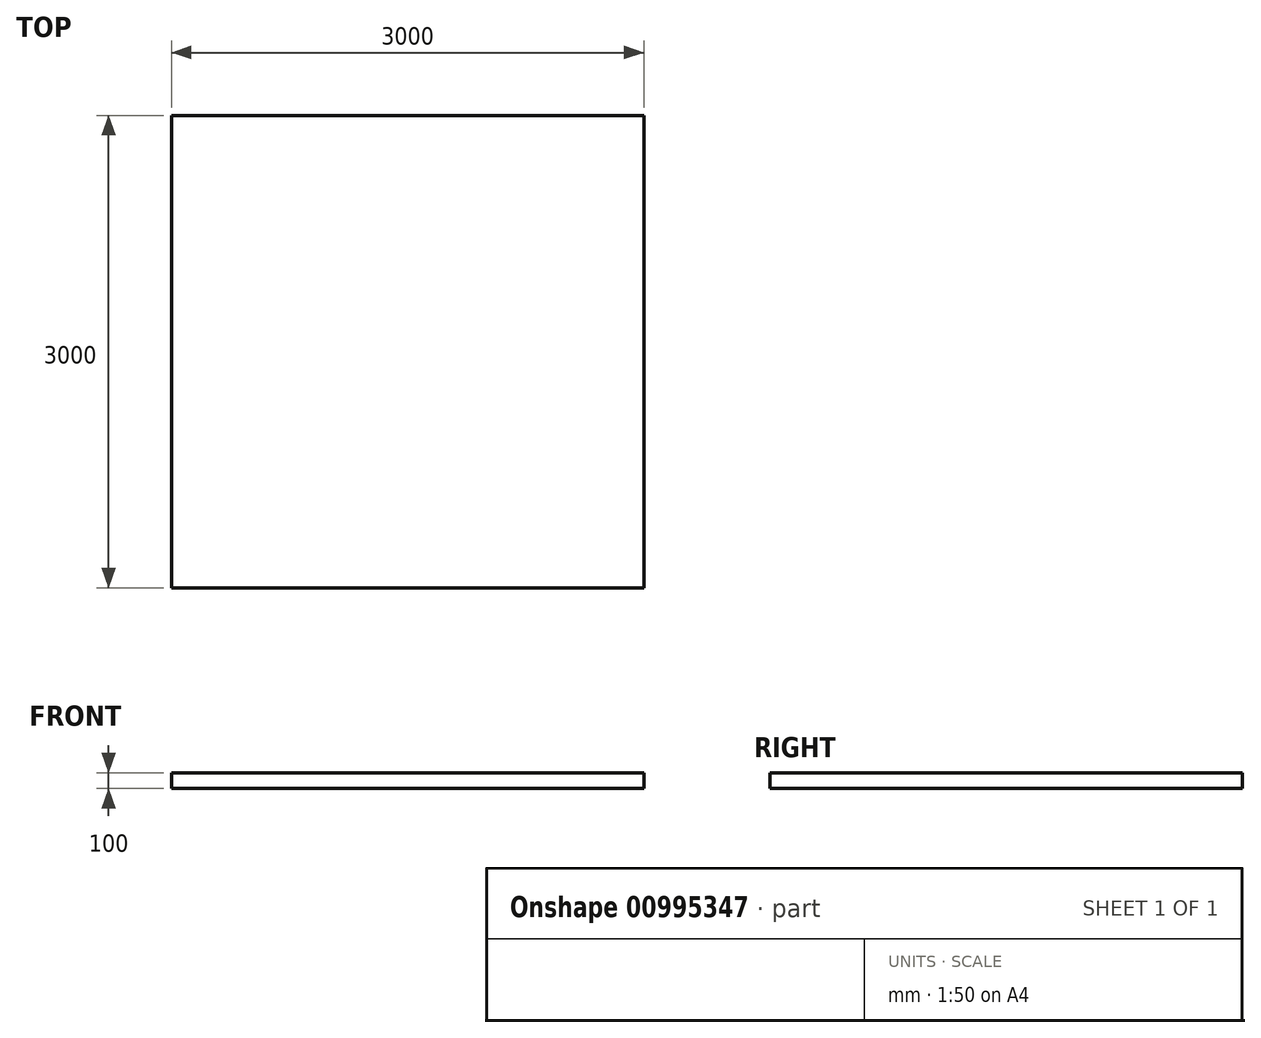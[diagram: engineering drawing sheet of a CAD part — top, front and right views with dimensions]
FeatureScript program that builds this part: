
annotation { "Feature Type Name" : "Feature", "Feature Type Description" : "" }
export const myFeature = defineFeature(function(context is Context, id is Id, definition is map)
    precondition{}
    {
        {
            var Q0;
            Q0=qCreatedBy(makeId("Top.planeOp"),FACE);
            var sketch = newSketch(context, id + "F0", { "sketchPlane" : qUnion([Q0])});
            skLineSegment(sketch, "E0.bottom", {"start": v(-1500, 1500) * mm, "end": v(1500, 1500) * mm});
            skLineSegment(sketch, "E0.top", {"start": v(-1500, -1500) * mm, "end": v(1500, -1500) * mm});
            skLineSegment(sketch, "E0.left", {"start": v(-1500, 1500) * mm, "end": v(-1500, -1500) * mm});
            skLineSegment(sketch, "E0.right", {"start": v(1500, 1500) * mm, "end": v(1500, -1500) * mm});
            skSolve(sketch);
        }
        {
            var Q0;
            Q0 = qSketchRegion(id + "F0", true);
            extrude(context, id + "F1", {"entities" : qUnion([Q0]), "depth" : 100 * mm, "offsetDistance" : 25 * mm});
        }
    });
